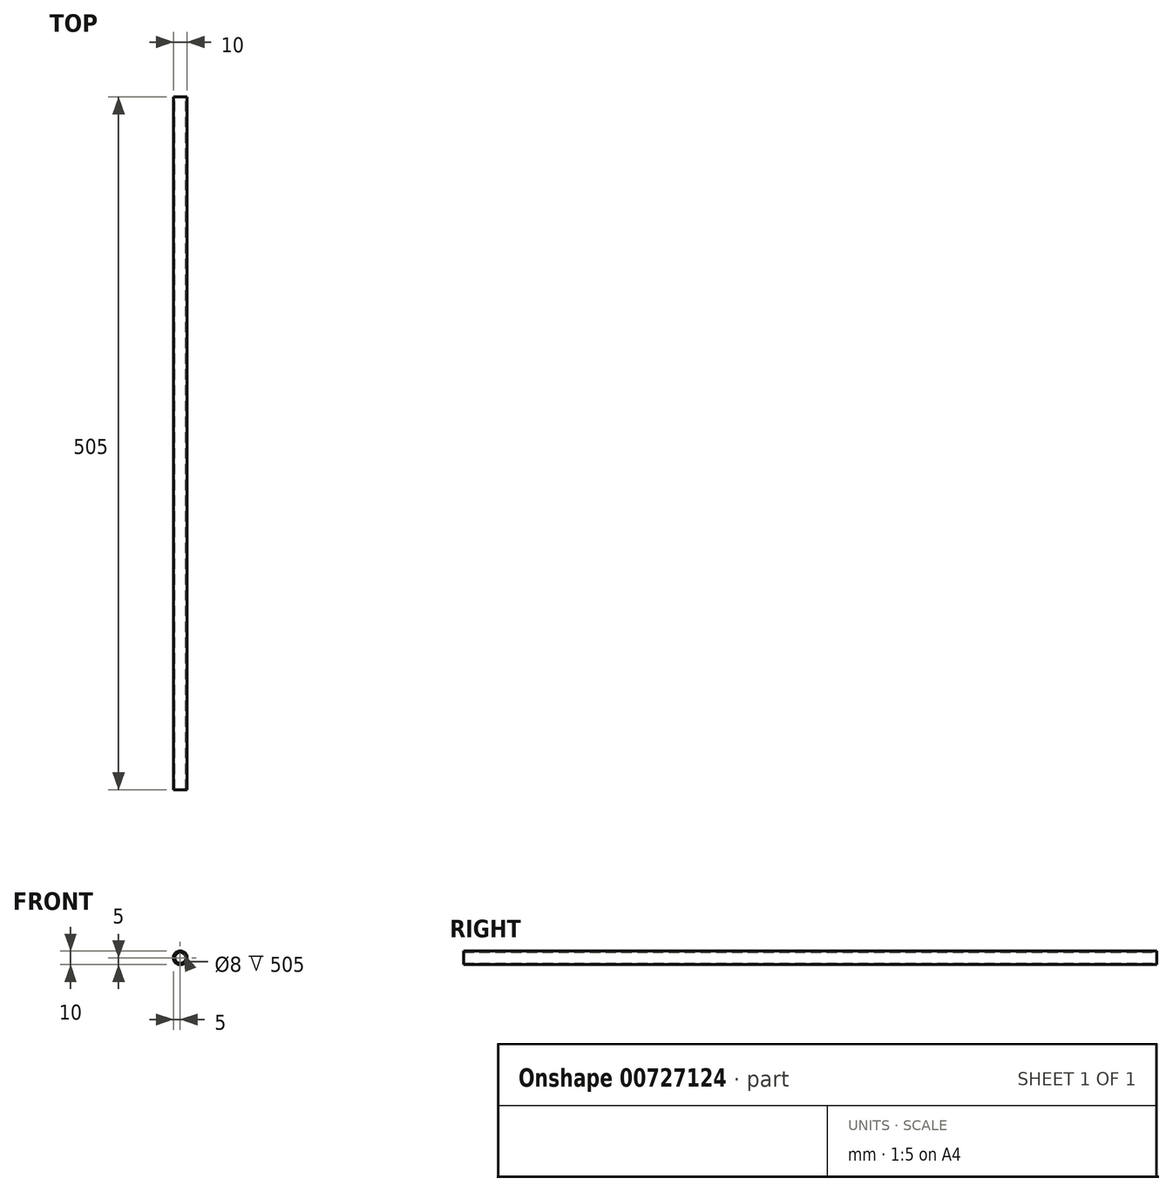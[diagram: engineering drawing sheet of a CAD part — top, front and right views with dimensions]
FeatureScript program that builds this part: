
annotation { "Feature Type Name" : "Feature", "Feature Type Description" : "" }
export const myFeature = defineFeature(function(context is Context, id is Id, definition is map)
    precondition{}
    {
        {
            var Q0;
            Q0=qCreatedBy(makeId("Front.planeOp"),FACE);
            var sketch = newSketch(context, id + "F0", { "sketchPlane" : qUnion([Q0])});
            skCircle(sketch, "E0", {"center": v(0, 0) * mm, "radius": 4 * mm});
            skCircle(sketch, "E1", {"center": v(0, 0) * mm, "radius": 5 * mm});
            skSolve(sketch);
        }
        {
            var Q0;
            Q0 = qSketchRegion(id + "F0", true);
            extrude(context, id + "F1", {"entities" : qUnion([Q0]), "depth" : 505 * mm, "offsetDistance" : 25 * mm});
        }
    });
